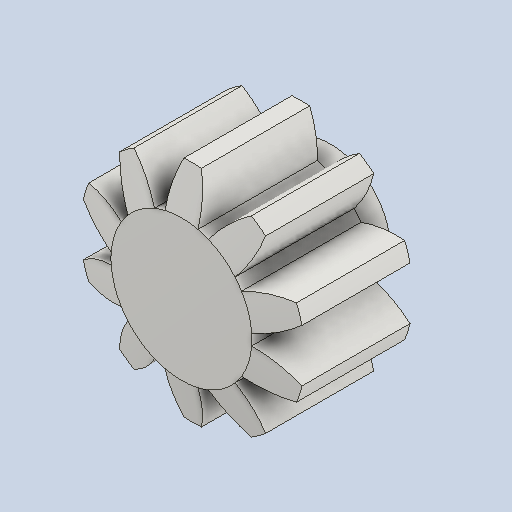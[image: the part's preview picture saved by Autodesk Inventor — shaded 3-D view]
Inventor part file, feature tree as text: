
AUTODESK INVENTOR PART (.ipt)
format: ipt  version: 2022 (Build 260153000, 153)  size: 281,088 bytes
history: native  units: in
note: dims shown in document units (in); Inventor stores cm internally (conversion verified against a paired STEP export)
features: other x12, sketch x6, plane x3
ambient origin geometry x8: Origin, YZ Plane, XZ Plane, XY Plane, X Axis, Y Axis, Z Axis, Center Point
bodies: Solid1 (feature_tree)
feature tree (21):
  other  "Spur Gear11_MIR.ipt"
  other  "Solid1::Spur Gear11_MIR.ipt"
  other  "TaggingFeature1"
  sketch  "Sketch1"  dims[d0=0.3937in]
  sketch  "Sketch2"  dims[d9=0.0in d14=0.0in d15=0.9352in d16=0.0in d17=0.0in d18=0.0in d19=0.9352in]
  sketch  "Sketch3"
  sketch  "Sketch4"
  sketch  "Sketch5"
  sketch  "Sketch6"
  plane  "XZ Plane_1"
  plane  "Work Plane2"
  plane  "Work Plane3"
  other  "Srf1"
  other  "Srf1::Derived"
  other  "Start plane iMate"
  other  "Distance iMate"
  other  "Position iMate"
  other  "Mesh iMate"
  other  "Axis iMate"
  other  "Mesh iMate2"
  other  "Align iMate"
